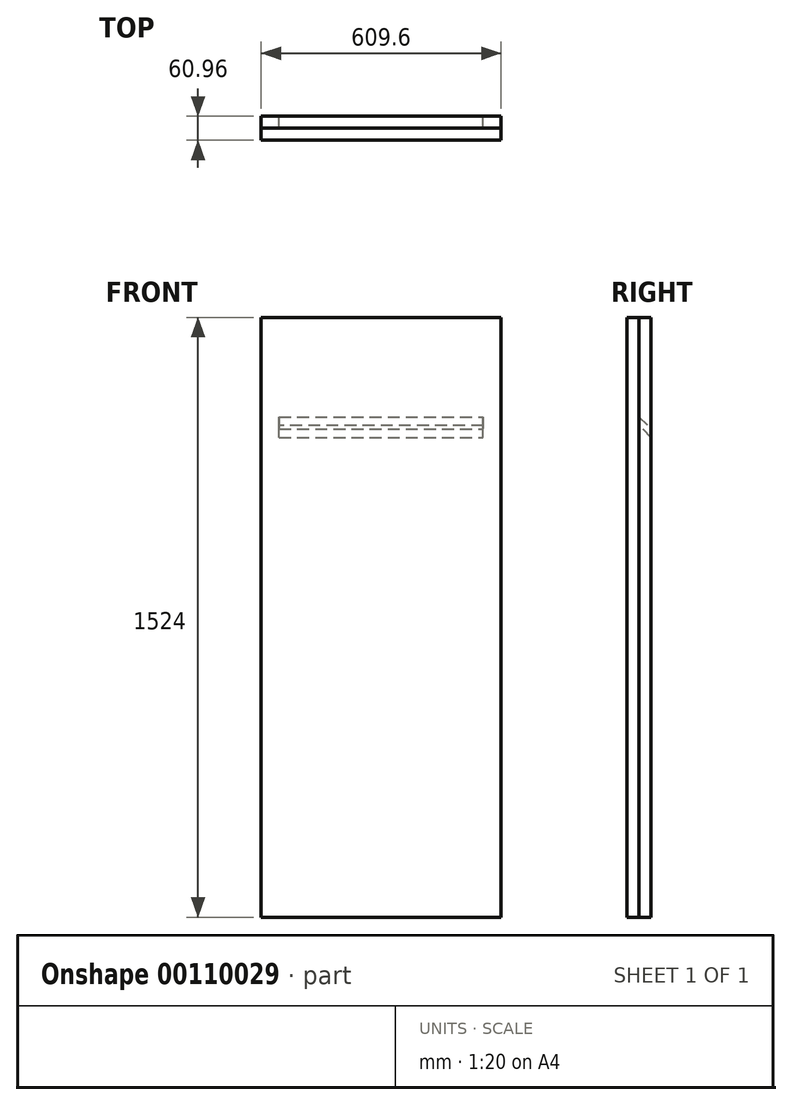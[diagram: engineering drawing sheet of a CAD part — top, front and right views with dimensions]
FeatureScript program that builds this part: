
annotation { "Feature Type Name" : "Feature", "Feature Type Description" : "" }
export const myFeature = defineFeature(function(context is Context, id is Id, definition is map)
    precondition{}
    {
        {
            var Q0;
            Q0=qCreatedBy(makeId("Front.planeOp"),FACE);
            var sketch = newSketch(context, id + "F0", { "sketchPlane" : qUnion([Q0])});
            skLineSegment(sketch, "E0.bottom", {"start": v(-304.8, 762) * mm, "end": v(304.8, 762) * mm});
            skLineSegment(sketch, "E0.top", {"start": v(-304.8, -762) * mm, "end": v(304.8, -762) * mm});
            skLineSegment(sketch, "E0.left", {"start": v(-304.8, 762) * mm, "end": v(-304.8, -762) * mm});
            skLineSegment(sketch, "E0.right", {"start": v(304.8, 762) * mm, "end": v(304.8, -762) * mm});
            skPoint(sketch, "E0.middle", {"position": v(0, 0) * mm});
            skSolve(sketch);
        }
        {
            var Q0;
            Q0 = qSketchRegion(id + "F0", true);
            extrude(context, id + "F1", {"entities" : qUnion([Q0]), "depth" : 30.48 * mm});
        }
        {
            var Q0;
            Q0=makeQuery(id+"F1.opExtrude","SWEPT_FACE",FACE,{"disambiguationData":[OSD([sQuery(id+"F0.wireOp",EDGE,"E0.right")])]});
            var sketch = newSketch(context, id + "F2", { "sketchPlane" : qUnion([Q0])});
            skLineSegment(sketch, "E1", {"start": v(0, -762) * mm, "end": v(0, 457.2) * mm, "construction": true});
            skLineSegment(sketch, "E2", {"start": v(0, 457.2) * mm, "end": v(-30.48, 487.68) * mm});
            skLineSegment(sketch, "E3", {"start": v(-30.48, 487.68) * mm, "end": v(-47.28, 504.48) * mm});
            skLineSegment(sketch, "E4", {"start": v(-47.28, 504.48) * mm, "end": v(-36.5, 515.25) * mm});
            skLineSegment(sketch, "E5", {"start": v(-36.5, 515.25) * mm, "end": v(11.94, 466.81) * mm});
            skLineSegment(sketch, "E6", {"start": v(11.94, 466.81) * mm, "end": v(0, 457.2) * mm});
            skSolve(sketch);
        }
        {
            var Q0;
            Q0 = qSketchRegion(id + "F2", true);
            extrude(context, id + "F3", {"entities" : qUnion([Q0]), "operationType" : NewBodyOperationType.REMOVE, "oppositeDirection" : true, "depth" : 609.6 * mm});
        }
        {
            var Q0;
            Q0=makeQuery(id+"F1.opExtrude","SWEPT_FACE",FACE,{"disambiguationData":[OSD([sQuery(id+"F0.wireOp",EDGE,"E0.bottom")])]});
            var sketch = newSketch(context, id + "F4", { "sketchPlane" : qUnion([Q0])});
            skLineSegment(sketch, "E7.bottom", {"start": v(-304.8, 0) * mm, "end": v(-259.08, 0) * mm});
            skLineSegment(sketch, "E7.top", {"start": v(-304.8, -30.48) * mm, "end": v(-259.08, -30.48) * mm});
            skLineSegment(sketch, "E7.left", {"start": v(-304.8, 0) * mm, "end": v(-304.8, -30.48) * mm});
            skLineSegment(sketch, "E7.right", {"start": v(-259.08, 0) * mm, "end": v(-259.08, -30.48) * mm});
            skLineSegment(sketch, "E8.bottom", {"start": v(304.8, 0) * mm, "end": v(259.08, 0) * mm});
            skLineSegment(sketch, "E8.top", {"start": v(304.8, -30.48) * mm, "end": v(259.08, -30.48) * mm});
            skLineSegment(sketch, "E8.left", {"start": v(304.8, 0) * mm, "end": v(304.8, -30.48) * mm});
            skLineSegment(sketch, "E8.right", {"start": v(259.08, 0) * mm, "end": v(259.08, -30.48) * mm});
            skSolve(sketch);
        }
        {
            var Q0;
            Q0 = qSketchRegion(id + "F4", true);
            extrude(context, id + "F5", {"entities" : qUnion([Q0]), "operationType" : NewBodyOperationType.ADD, "oppositeDirection" : true, "depth" : 609.6 * mm});
        }
        {
            var Q0;
            {var subQ0=sQuery(id+"F0.wireOp",EDGE,"E0.top");var subQ1=sQuery(id+"F0.wireOp",EDGE,"E0.left");var subQ3=sQuery(id+"F0.wireOp",EDGE,"E0.right");var subQ5=sQuery(id+"F0.wireOp",EDGE,"E0.bottom");var subQ6=makeQuery(id+"F1.opExtrude","CAP_FACE",FACE,{"disambiguationData":[OSD([subQ5,subQ0,subQ1,subQ3])],"isStart":false});Q0=makeQuery(id+"F5.boolean.opBoolean","MERGE",FACE,{"derivedFrom":[makeQuery(id+"F3.boolean.opBoolean","SPLIT",FACE,{"disambiguationData":[TD([makeQuery(id+"F1.opExtrude","SWEPT_FACE",FACE,{"disambiguationData":[OSD([subQ5])]})])],"derivedFrom":subQ6}),makeQuery(id+"F3.boolean.opBoolean","SPLIT",FACE,{"disambiguationData":[TD([makeQuery(id+"F1.opExtrude","SWEPT_FACE",FACE,{"disambiguationData":[OSD([subQ0])]})])],"derivedFrom":subQ6}),makeQuery(id+"F5.opExtrude","SWEPT_FACE",FACE,{"disambiguationData":[OSD([sQuery(id+"F4.wireOp",EDGE,"E7.top")])]}),makeQuery(id+"F5.opExtrude","SWEPT_FACE",FACE,{"disambiguationData":[OSD([sQuery(id+"F4.wireOp",EDGE,"E8.top")])]})]});}
            var sketch = newSketch(context, id + "F6", { "sketchPlane" : qUnion([Q0])});
            skLineSegment(sketch, "E9.bottom", {"start": v(-304.8, 762) * mm, "end": v(304.8, 762) * mm});
            skLineSegment(sketch, "E9.top", {"start": v(-304.8, -762) * mm, "end": v(304.8, -762) * mm});
            skLineSegment(sketch, "E9.left", {"start": v(-304.8, 762) * mm, "end": v(-304.8, -762) * mm});
            skLineSegment(sketch, "E9.right", {"start": v(304.8, 762) * mm, "end": v(304.8, -762) * mm});
            skSolve(sketch);
        }
        {
            var Q0;
            Q0 = qSketchRegion(id + "F6", true);
            extrude(context, id + "F7", {"entities" : qUnion([Q0]), "depth" : 30.48 * mm});
        }
    });
